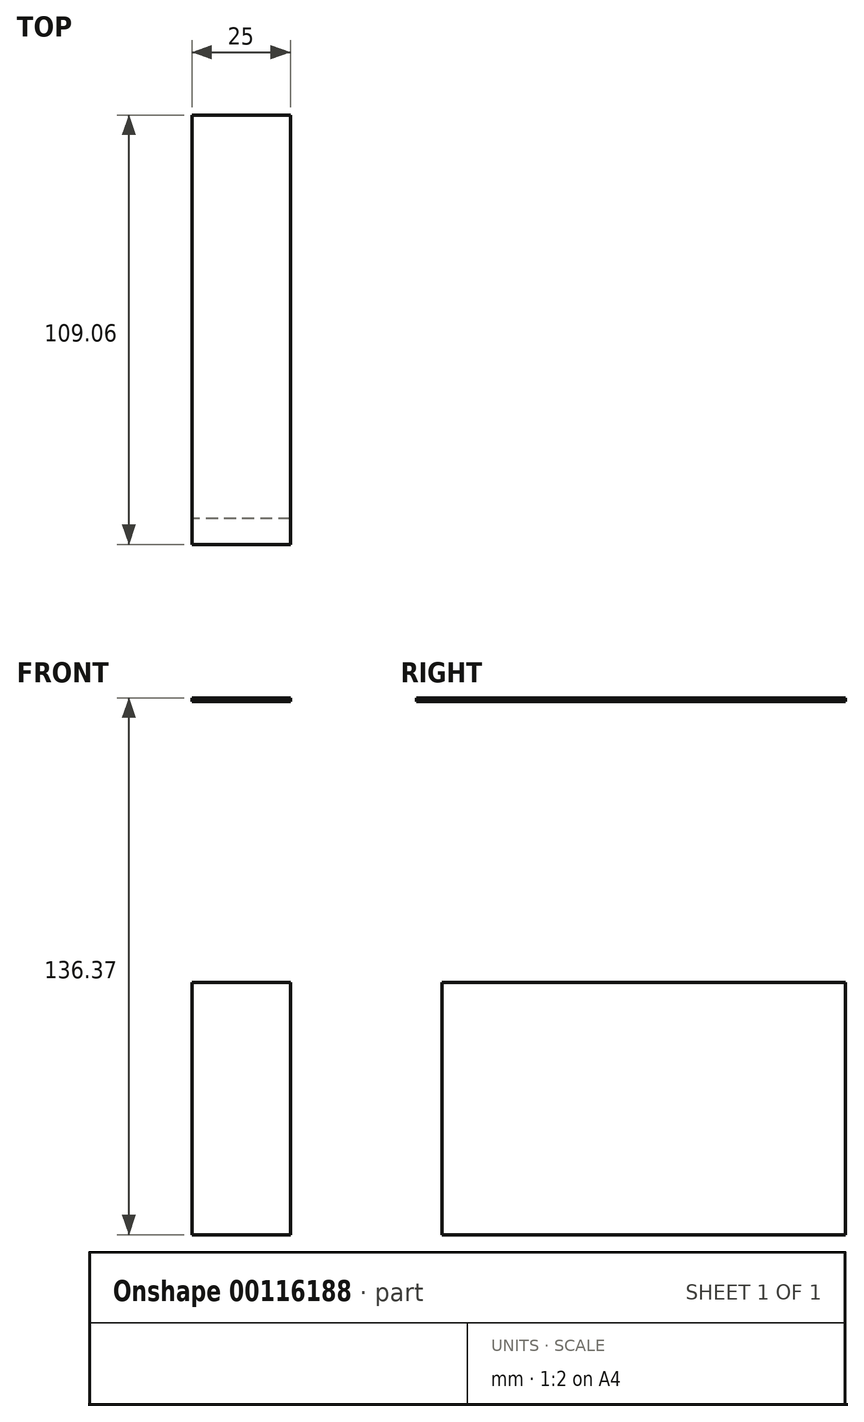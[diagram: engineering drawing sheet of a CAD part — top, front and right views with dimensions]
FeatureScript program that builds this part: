
annotation { "Feature Type Name" : "Feature", "Feature Type Description" : "" }
export const myFeature = defineFeature(function(context is Context, id is Id, definition is map)
    precondition{}
    {
        {
            var Q0;
            Q0=qCreatedBy(makeId("Right.planeOp"),FACE);
            var sketch = newSketch(context, id + "F0", { "sketchPlane" : qUnion([Q0])});
            skLineSegment(sketch, "E0.bottom", {"start": v(0, 71.37) * mm, "end": v(-109.06, 71.37) * mm});
            skLineSegment(sketch, "E0.top", {"start": v(0, 72.3) * mm, "end": v(-109.06, 72.3) * mm});
            skLineSegment(sketch, "E0.left", {"start": v(0, 71.37) * mm, "end": v(0, 72.3) * mm});
            skLineSegment(sketch, "E0.right", {"start": v(-109.06, 71.37) * mm, "end": v(-109.06, 72.3) * mm});
            skLineSegment(sketch, "E1.bottom", {"start": v(-102.48, 0) * mm, "end": v(0, 0) * mm});
            skLineSegment(sketch, "E1.top", {"start": v(-102.48, -64.08) * mm, "end": v(0, -64.08) * mm});
            skLineSegment(sketch, "E1.left", {"start": v(-102.48, 0) * mm, "end": v(-102.48, -64.08) * mm});
            skLineSegment(sketch, "E1.right", {"start": v(0, 0) * mm, "end": v(0, -64.08) * mm});
            skSolve(sketch);
        }
        {
            var Q0;
            Q0=makeQuery(id+"F0.imprint","IMPRINT",FACE,{"disambiguationData":[TD([[makeQuery(id+"F0.imprint","IMPRINT",EDGE,{"derivedFrom":sQuery(id+"F0.wireOp",EDGE,"E1.bottom")}),-1.0]])]});
            var Q1;
            Q1 = qSketchRegion(id + "F0", true);
            extrude(context, id + "F1", {"entities" : qUnion([Q0, Q1]), "depth" : 25 * mm});
        }
    });
